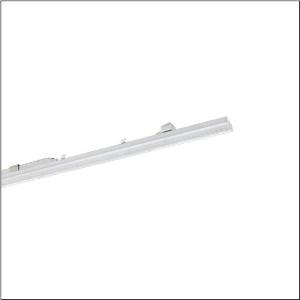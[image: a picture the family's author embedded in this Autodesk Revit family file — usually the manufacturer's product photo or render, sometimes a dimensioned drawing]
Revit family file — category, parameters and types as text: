
# Revit family: tl_l_5wd7a8h0g2b5
name_source: partatom
category: Lighting Fixtures
units: mm (PartAtom-declared; Revit-internal decimal feet)

## family parameters
Cut with Voids When Loaded = No
Host = Face
Light Source = No
Part Type = Normal
Room Calculation Point = No
Round Connector Dimension = Use Diameter
Shared = No

## types (1)
- --- (1 x LED, 850 lm, 4.5 W, 4000K)
    Apparent Load = 5 VA
    CIE Flux Codes = 49 84 98 100 100
    Color Rendering = 80
    Color Temperature = 4000K
    Default Elevation = 1800 mm
    Description = TL L, luminaire insert, of sheet steel, galvanised, coil coated, white, length: 1.500mm, width: 66mm, height: 67mm, surge protection,LED rated luminous flux: 4.990lm, light colour: 840, control gear: emergency light, with terminal, 3-pole, mains connection: 230..240V, AC, 50/60Hz, rated input power: 34W, primary optical cover: cover, of PMMA, light emission: direct distribution, protection rating (complete): as luminaire, insulation class (complete): insulation class I (protective earthing), certification: CE, impact resistance: IK06, permissible ambient temperature for indoor applications: +5..+35°C, packaging unit: 1 piece
    Height = 120 mm
    Lamp = 1 x LED
    Lamp Light Flux = 850 lm
    Lamp Power = 4.5 W
    Lamp count = 1
    Length = 1690 mm
    Luminous efficacy = 189 lm/W
    Manufacturer = Siteco
    ModVariant = No
    Model = 5WD7A8H0G2B5
    Mounting Place = Ceiling
    Mounting Type = Pendant
    Number of Poles = 1
    OnlyDefault = Yes
    Power Factor = 1
    Product Name = TL L
    Product group = luminaire insert
    ProductGroupID = 901
    Protection Class = Protection class I
    Protection Degree = Degree of protection
    RLX_Detail_Level = 1
    RLX_Emergency_Light_Flux = 0 lm
    RLX_Emergency_Type = 0
    RLX_Emergency_Type_DB = No
    RlxData = <blob elided: 17405 chars, md5=c618f34b>
    Socket = socket
    Standby Power = 0 W
    System Light Flux = 850 lm
    System Power = 5 W
    Type Comments = : emergency light operation: 3 h
    Type Image = l_1294382.jpg
    URL = http://relux.com
    VarID = @adj_012045
    Voltage = 0 V
    Weight = 0.00 kg
    Width = 208 mm

## geometry (parser evidence)
native form markers: Blend x4, Sweep x11
no freeform markers — native parametric forms only
